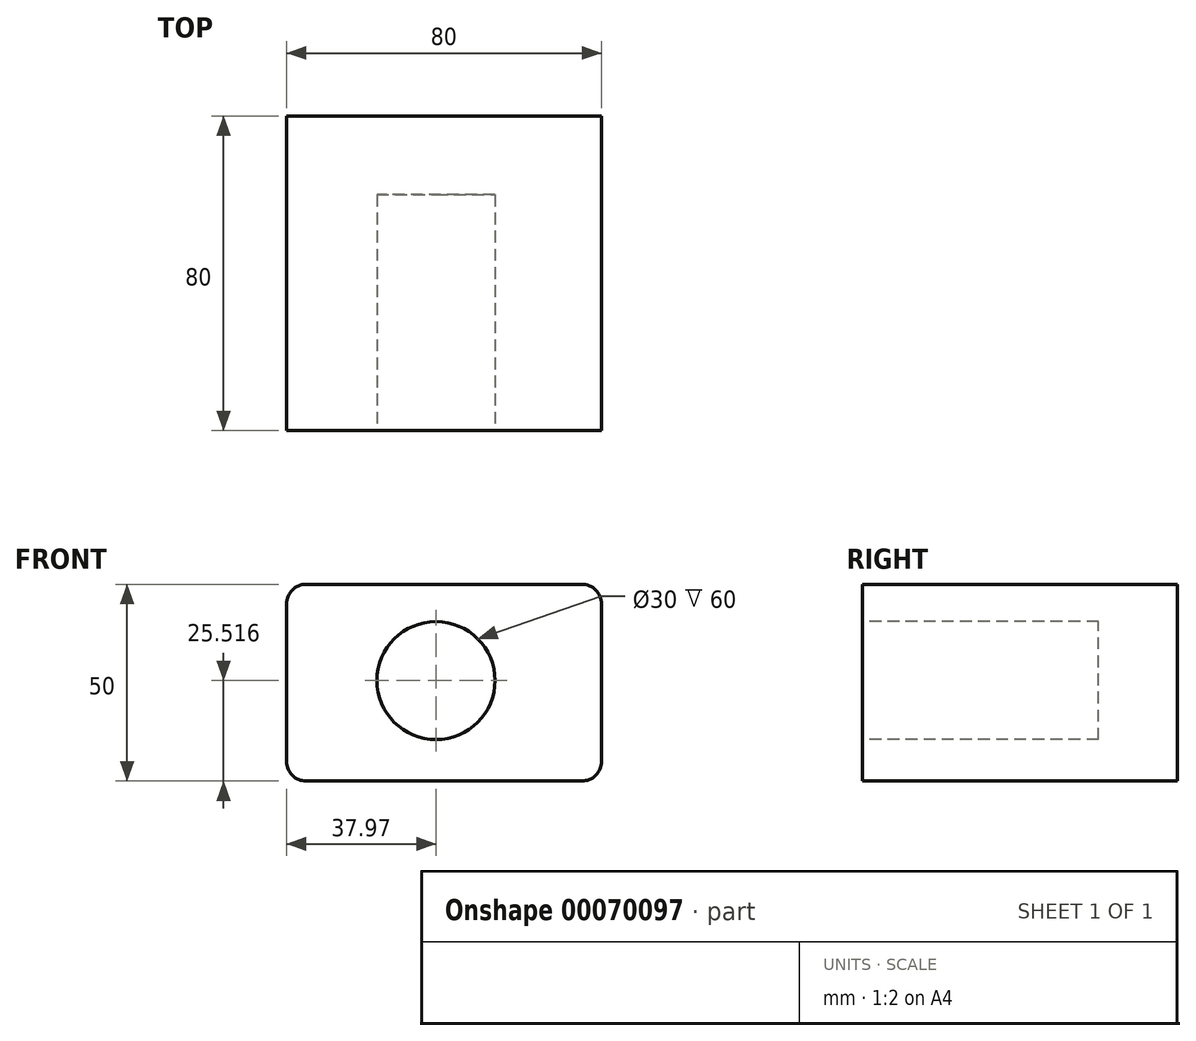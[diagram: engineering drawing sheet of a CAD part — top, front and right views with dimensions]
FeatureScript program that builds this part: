
annotation { "Feature Type Name" : "Feature", "Feature Type Description" : "" }
export const myFeature = defineFeature(function(context is Context, id is Id, definition is map)
    precondition{}
    {
        {
            var Q0;
            Q0=qCreatedBy(makeId("Front.planeOp"),FACE);
            var sketch = newSketch(context, id + "F0", { "sketchPlane" : qUnion([Q0])});
            skLineSegment(sketch, "E0.bottom", {"start": v(-37.97, 28.79) * mm, "end": v(42.03, 28.79) * mm});
            skLineSegment(sketch, "E0.top", {"start": v(-37.97, -21.21) * mm, "end": v(42.03, -21.21) * mm});
            skLineSegment(sketch, "E0.left", {"start": v(-37.97, 28.79) * mm, "end": v(-37.97, -21.21) * mm});
            skLineSegment(sketch, "E0.right", {"start": v(42.03, 28.79) * mm, "end": v(42.03, -21.21) * mm});
            skSolve(sketch);
        }
        {
            var Q0;
            Q0=makeQuery(id+"F0.imprint","IMPRINT",FACE,{"disambiguationData":[TD([[makeQuery(id+"F0.imprint","IMPRINT",EDGE,{"derivedFrom":sQuery(id+"F0.wireOp",EDGE,"E0.bottom")}),-1.0]])]});
            extrude(context, id + "F1", {"entities" : qUnion([Q0]), "depth" : 80 * mm});
        }
        {
            var Q0;
            Q0=makeQuery(id+"F1.opExtrude","CAP_FACE",FACE,{"disambiguationData":[OSD([sQuery(id+"F0.wireOp",EDGE,"E0.bottom"),sQuery(id+"F0.wireOp",EDGE,"E0.top"),sQuery(id+"F0.wireOp",EDGE,"E0.left"),sQuery(id+"F0.wireOp",EDGE,"E0.right")])],"isStart":false});
            var sketch = newSketch(context, id + "F2", { "sketchPlane" : qUnion([Q0])});
            skCircle(sketch, "E1", {"center": v(0, 4.3) * mm, "radius": 15 * mm});
            skSolve(sketch);
        }
        {
            var Q0;
            Q0=makeQuery(id+"F2.imprint","IMPRINT",FACE,{"disambiguationData":[TD([[makeQuery(id+"F2.imprint","IMPRINT",EDGE,{"derivedFrom":sQuery(id+"F2.wireOp",EDGE,"E1")}),1.0]])]});
            extrude(context, id + "F3", {"entities" : qUnion([Q0]), "operationType" : NewBodyOperationType.REMOVE, "oppositeDirection" : true, "depth" : 60 * mm});
        }
        {
            var Q0;
            Q0=makeQuery(id+"F1.opExtrude","SWEPT_EDGE",EDGE,{"disambiguationData":[OSD([sQuery(id+"F0.wireOp",EDGE,"E0.bottom"),sQuery(id+"F0.wireOp",EDGE,"E0.left")])]});
            var Q1;
            Q1=makeQuery(id+"F1.opExtrude","SWEPT_EDGE",EDGE,{"disambiguationData":[OSD([sQuery(id+"F0.wireOp",EDGE,"E0.bottom"),sQuery(id+"F0.wireOp",EDGE,"E0.right")])]});
            var Q2;
            Q2=makeQuery(id+"F1.opExtrude","SWEPT_EDGE",EDGE,{"disambiguationData":[OSD([sQuery(id+"F0.wireOp",EDGE,"E0.top"),sQuery(id+"F0.wireOp",EDGE,"E0.left")])]});
            var Q3;
            Q3=makeQuery(id+"F1.opExtrude","SWEPT_EDGE",EDGE,{"disambiguationData":[OSD([sQuery(id+"F0.wireOp",EDGE,"E0.top"),sQuery(id+"F0.wireOp",EDGE,"E0.right")])]});
            fillet(context, id + "F4", {"entities" : qUnion([Q0, Q1, Q2, Q3]), "radius" : 5 * mm, "tangentPropagation" : true, "allowEdgeOverflow" : false});
        }
    });
